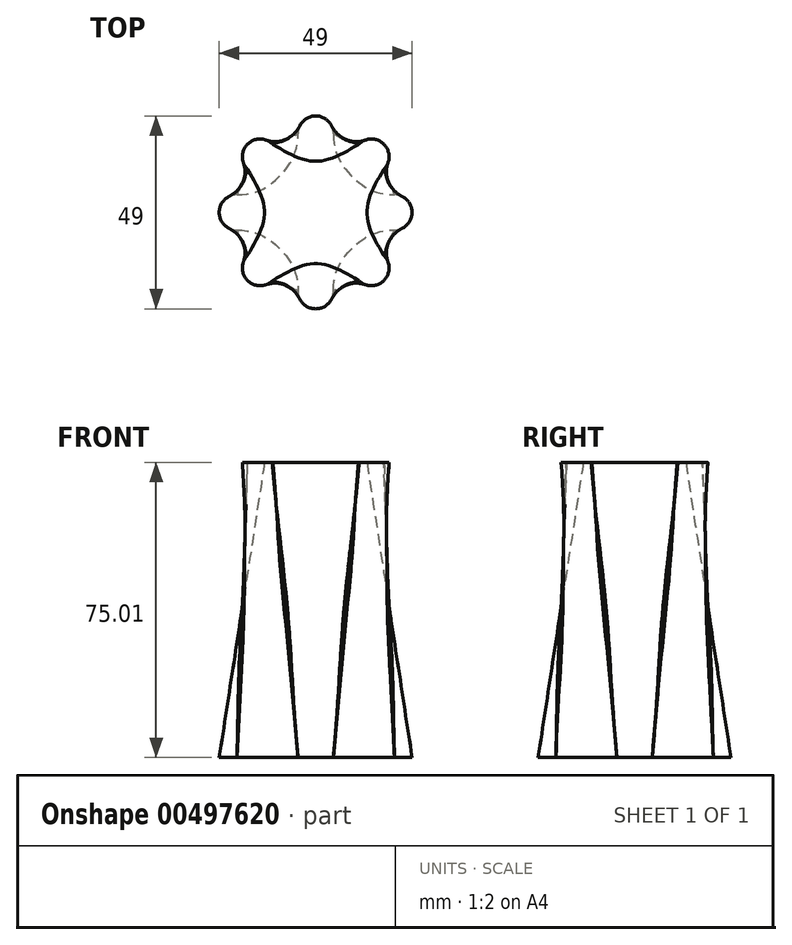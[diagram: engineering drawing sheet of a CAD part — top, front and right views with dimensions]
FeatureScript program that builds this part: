
annotation { "Feature Type Name" : "Feature", "Feature Type Description" : "" }
export const myFeature = defineFeature(function(context is Context, id is Id, definition is map)
    precondition{}
    {
        {
            var Q0;
            Q0=qCreatedBy(makeId("Top.planeOp"),FACE);
            var sketch = newSketch(context, id + "F0", { "sketchPlane" : qUnion([Q0])});
            skLineSegment(sketch, "E0", {"start": v(0, 0) * mm, "end": v(0, 20) * mm});
            skArc(sketch, "E1", {"start": v(4.5, 20) * mm, "mid": v(0, 24.5) * mm, "end": v(-4.5, 20) * mm});
            skArc(sketch, "E2", {"start": v(20, -4.5) * mm, "mid": v(24.5, 0) * mm, "end": v(20, 4.5) * mm});
            skArc(sketch, "E3.MirrorC", {"start": v(-20, -4.5) * mm, "mid": v(-24.5, 0) * mm, "end": v(-20, 4.5) * mm});
            skArc(sketch, "E4.MirrorC", {"start": v(4.5, -20) * mm, "mid": v(0, -24.5) * mm, "end": v(-4.5, -20) * mm});
            skLineSegment(sketch, "E5", {"start": v(5, 5) * mm, "end": v(10, 0) * mm});
            skPoint(sketch, "E6", {"position": v(4.5, 20) * mm});
            skPoint(sketch, "E7", {"position": v(20, 4.5) * mm});
            skFitSpline(sketch, "E8", {"points": [v(4.5, 20) * mm, v(9.2, 9.2) * mm, v(20, 4.5) * mm], "startDerivative": vector(-0.04, -31.04) * mm, "endDerivative": vector(31.04, 0.04) * mm});
            skPoint(sketch, "E9.MirrorP", {"position": v(-4.5, 20) * mm});
            skPoint(sketch, "E10.MirrorP", {"position": v(-20, 4.5) * mm});
            skFitSpline(sketch, "E11", {"points": [v(-20, 4.5) * mm, v(-9.2, 9.2) * mm, v(-4.5, 20) * mm], "startDerivative": vector(31.04, -0.04) * mm, "endDerivative": vector(-0.04, 31.04) * mm});
            skFitSpline(sketch, "E12.MirrorCS", {"points": [v(-20, -4.5) * mm, v(-9.2, -9.2) * mm, v(-4.5, -20) * mm], "startDerivative": vector(31.04, 0.04) * mm, "endDerivative": vector(-0.04, -31.04) * mm});
            skFitSpline(sketch, "E13.MirrorCS", {"points": [v(4.5, -20) * mm, v(9.2, -9.2) * mm, v(20, -4.5) * mm], "startDerivative": vector(-0.04, 31.04) * mm, "endDerivative": vector(31.04, -0.04) * mm});
            skPoint(sketch, "E14.orphan", {"position": v(0, 10) * mm});
            skSolve(sketch);
        }
        {
            var Q0;
            Q0=qCreatedBy(makeId("Top.planeOp"),FACE);
            cPlane(context, id + "F1", {"entities" : qUnion([Q0]), "cplaneType" : CPlaneType.OFFSET, "offset" : 75 * mm, "width" : 150 * mm, "height" : 150 * mm});
        }
        {
            var Q0;
            Q0=qCreatedBy(id+"F1.planeOp",FACE);
            var sketch = newSketch(context, id + "F2", { "sketchPlane" : qUnion([Q0])});
            skLineSegment(sketch, "E15", {"start": v(0, 0) * mm, "end": v(14.14, 14.14) * mm});
            skArc(sketch, "E16", {"start": v(17.32, 10.96) * mm, "mid": v(17.32, 17.32) * mm, "end": v(10.96, 17.32) * mm});
            skPoint(sketch, "E17", {"position": v(10.96, 17.32) * mm});
            skPoint(sketch, "E18.MirrorP", {"position": v(17.32, 10.96) * mm});
            skArc(sketch, "E19.MirrorC", {"start": v(-17.32, 10.96) * mm, "mid": v(-17.32, 17.32) * mm, "end": v(-10.96, 17.32) * mm});
            skPoint(sketch, "E20.MirrorP", {"position": v(-10.96, 17.32) * mm});
            skPoint(sketch, "E21.MirrorP", {"position": v(-17.32, 10.96) * mm});
            skPoint(sketch, "E22.MirrorP", {"position": v(-17.32, -10.96) * mm});
            skPoint(sketch, "E23.MirrorP", {"position": v(-10.96, -17.32) * mm});
            skArc(sketch, "E24.MirrorCS", {"start": v(-17.32, -10.96) * mm, "mid": v(-17.32, -17.32) * mm, "end": v(-10.96, -17.32) * mm});
            skPoint(sketch, "E25.MirrorP", {"position": v(10.96, -17.32) * mm});
            skPoint(sketch, "E26.MirrorP", {"position": v(17.32, -10.96) * mm});
            skArc(sketch, "E27.MirrorCS", {"start": v(17.32, -10.96) * mm, "mid": v(17.32, -17.32) * mm, "end": v(10.96, -17.32) * mm});
            skFitSpline(sketch, "E28", {"points": [v(-10.96, 17.32) * mm, v(0, 13) * mm, v(10.96, 17.32) * mm], "startDerivative": vector(21.92, -12.97) * mm, "endDerivative": vector(21.92, 12.97) * mm});
            skFitSpline(sketch, "E29.MirrorCS", {"points": [v(17.32, -10.96) * mm, v(13, 0) * mm, v(17.32, 10.96) * mm], "startDerivative": vector(-12.97, 21.92) * mm, "endDerivative": vector(12.97, 21.92) * mm});
            skFitSpline(sketch, "E30.MirrorCS", {"points": [v(10.96, -17.32) * mm, v(0, -13) * mm, v(-10.96, -17.32) * mm], "startDerivative": vector(-21.92, 12.97) * mm, "endDerivative": vector(-21.92, -12.97) * mm});
            skFitSpline(sketch, "E31.MirrorCS", {"points": [v(-17.32, 10.96) * mm, v(-13, 0) * mm, v(-17.32, -10.96) * mm], "startDerivative": vector(12.97, -21.92) * mm, "endDerivative": vector(-12.97, -21.92) * mm});
            skSolve(sketch);
        }
        {
            var Q0;
            Q0=makeQuery(id+"F0.imprint","IMPRINT",FACE,{"disambiguationData":[TD([[makeQuery(id+"F0.imprint","IMPRINT",EDGE,{"derivedFrom":sQuery(id+"F0.wireOp",EDGE,"E1")}),1.0]])]});
            var Q1;
            Q1=makeQuery(id+"F2.imprint","IMPRINT",FACE,{"disambiguationData":[TD([[makeQuery(id+"F2.imprint","IMPRINT",EDGE,{"derivedFrom":sQuery(id+"F2.wireOp",EDGE,"E16")}),1.0]])]});
            var Q2;
            Q2=sQuery(id+"F0.wireOp",VERTEX,"E8.1.internal");
            var Q3;
            Q3=sQuery(id+"F2.wireOp",VERTEX,"fZQEgL5u-Hg5Y-vtmR-KdhO-cswhtPvZJIKj.end");
            loft(context, id + "F3", {"sheetProfilesArray" : [{ "sheetProfileEntities" : qUnion([Q0]) }, { "sheetProfileEntities" : qUnion([Q1]) }], "connections" : [{ "connectionEntities" : qUnion([Q2, Q3]), "connectionEdgeQueries" : qUnion([]), "connectionEdgeParameters" : [] }]});
        }
        {
            var Q0;
            Q0=makeQuery(id+"F3.opLoft","SWEPT_EDGE",EDGE,{"disambiguationData":[OSD([sQuery(id+"F0.wireOp",EDGE,"E4.MirrorC"),sQuery(id+"F0.wireOp",EDGE,"E13.MirrorCS"),sQuery(id+"F2.wireOp",EDGE,"JJ1tIzN7-kO3n-YF0G-K4hK-3enDRhxHHEvD"),sQuery(id+"F2.wireOp",EDGE,"f9b304ae-1976-4873-9a5a-c5923a0547b1")])]});
            var Q1;
            Q1=makeQuery(id+"F3.opLoft","SWEPT_EDGE",EDGE,{"disambiguationData":[OSD([sQuery(id+"F0.wireOp",EDGE,"E2"),sQuery(id+"F0.wireOp",EDGE,"E13.MirrorCS"),sQuery(id+"F2.wireOp",EDGE,"JJ1tIzN7-kO3n-YF0G-K4hK-3enDRhxHHEvD"),sQuery(id+"F2.wireOp",EDGE,"33bcb077-760a-4651-b137-1f3f9d7b46e70.MirrorCS")])]});
            var Q2;
            Q2=makeQuery(id+"F3.opLoft","SWEPT_EDGE",EDGE,{"disambiguationData":[OSD([sQuery(id+"F0.wireOp",EDGE,"E2"),sQuery(id+"F0.wireOp",EDGE,"E8"),sQuery(id+"F2.wireOp",EDGE,"28cb81f7-611a-414f-a1e8-53eeff27f6270.MirrorC"),sQuery(id+"F2.wireOp",EDGE,"33bcb077-760a-4651-b137-1f3f9d7b46e70.MirrorCS")])]});
            fillet(context, id + "F4", {"entities" : qUnion([Q0, Q1, Q2]), "radius" : 1 * mm, "tangentPropagation" : true, "allowEdgeOverflow" : false});
        }
        {
            var Q0;
            Q0=makeQuery(id+"F3.opLoft","SWEPT_EDGE",EDGE,{"disambiguationData":[OSD([sQuery(id+"F0.wireOp",EDGE,"E1"),sQuery(id+"F0.wireOp",EDGE,"E8"),sQuery(id+"F2.wireOp",EDGE,"28cb81f7-611a-414f-a1e8-53eeff27f6270.MirrorC"),sQuery(id+"F2.wireOp",EDGE,"6abea538-f12b-45c5-872e-5a8fc1f25e5e0.MirrorCS")])]});
            var Q1;
            Q1=makeQuery(id+"F3.opLoft","SWEPT_EDGE",EDGE,{"disambiguationData":[OSD([sQuery(id+"F0.wireOp",EDGE,"E1"),sQuery(id+"F0.wireOp",EDGE,"E11"),sQuery(id+"F2.wireOp",EDGE,"6abea538-f12b-45c5-872e-5a8fc1f25e5e0.MirrorCS"),sQuery(id+"F2.wireOp",EDGE,"77ea4d05-b368-4faa-83fa-44a01390cedf0.MirrorC")])]});
            var Q2;
            Q2=makeQuery(id+"F3.opLoft","SWEPT_EDGE",EDGE,{"disambiguationData":[OSD([sQuery(id+"F0.wireOp",EDGE,"E3.MirrorC"),sQuery(id+"F0.wireOp",EDGE,"E11"),sQuery(id+"F2.wireOp",EDGE,"77ea4d05-b368-4faa-83fa-44a01390cedf0.MirrorC"),sQuery(id+"F2.wireOp",EDGE,"b79dfb3b-4546-4d59-b3ac-9f6bfab27c580.MirrorCS")])]});
            fillet(context, id + "F5", {"entities" : qUnion([Q0, Q1, Q2]), "radius" : 1 * mm, "tangentPropagation" : true, "allowEdgeOverflow" : false});
        }
        {
            var Q0;
            Q0=makeQuery(id+"F3.opLoft","SWEPT_EDGE",EDGE,{"disambiguationData":[OSD([sQuery(id+"F0.wireOp",EDGE,"E4.MirrorC"),sQuery(id+"F0.wireOp",EDGE,"E12.MirrorCS"),sQuery(id+"F2.wireOp",EDGE,"Ib4wRStb-wTvP-PisM-8EKu-hH2DSxwiwy4f"),sQuery(id+"F2.wireOp",EDGE,"f9b304ae-1976-4873-9a5a-c5923a0547b1")])]});
            var Q1;
            Q1=makeQuery(id+"F3.opLoft","SWEPT_EDGE",EDGE,{"disambiguationData":[OSD([sQuery(id+"F0.wireOp",EDGE,"E3.MirrorC"),sQuery(id+"F0.wireOp",EDGE,"E12.MirrorCS"),sQuery(id+"F2.wireOp",EDGE,"Ib4wRStb-wTvP-PisM-8EKu-hH2DSxwiwy4f"),sQuery(id+"F2.wireOp",EDGE,"b79dfb3b-4546-4d59-b3ac-9f6bfab27c580.MirrorCS")])]});
            fillet(context, id + "F6", {"entities" : qUnion([Q0, Q1]), "radius" : 1 * mm, "tangentPropagation" : true, "allowEdgeOverflow" : false});
        }
    });
